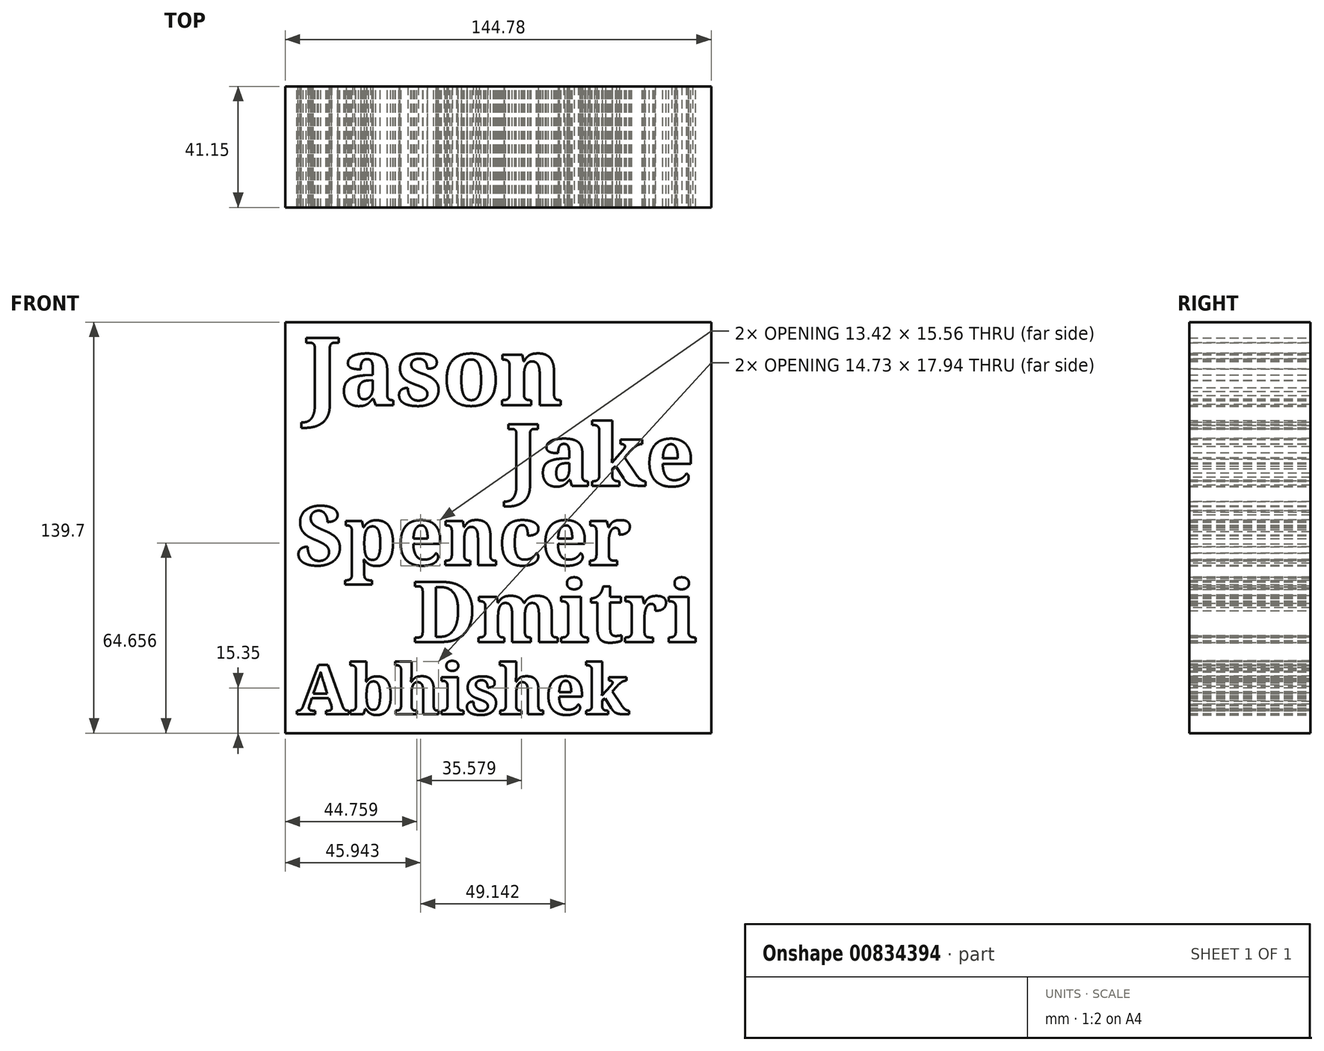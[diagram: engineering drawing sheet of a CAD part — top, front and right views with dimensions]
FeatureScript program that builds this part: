
annotation { "Feature Type Name" : "Feature", "Feature Type Description" : "" }
export const myFeature = defineFeature(function(context is Context, id is Id, definition is map)
    precondition{}
    {
        {
            var Q0;
            Q0=qCreatedBy(makeId("Front.planeOp"),FACE);
            var sketch = newSketch(context, id + "F0", { "sketchPlane" : qUnion([Q0])});
            skLineSegment(sketch, "E0.bottom", {"start": v(72.4, -69.85) * mm, "end": v(-72.39, -69.85) * mm});
            skLineSegment(sketch, "E0.top", {"start": v(72.39, 69.85) * mm, "end": v(-72.4, 69.85) * mm});
            skLineSegment(sketch, "E0.left", {"start": v(72.4, -69.85) * mm, "end": v(72.39, 69.85) * mm});
            skLineSegment(sketch, "E0.right", {"start": v(-72.39, -69.85) * mm, "end": v(-72.4, 69.85) * mm});
            skPoint(sketch, "E0.middle", {"position": v(0, 0) * mm});
            skText(sketch, "E1", { "text": "Jason", "fontName": "NotoSerif-Bold.ttf"});
            skText(sketch, "E2", { "text": "Jake", "fontName": "NotoSerif-Bold.ttf"});
            skText(sketch, "E3", { "text": "Spencer", "fontName": "NotoSerif-Bold.ttf"});
            skText(sketch, "E4", { "text": "Abhishek", "fontName": "NotoSerif-Bold.ttf"});
            skText(sketch, "E5", { "text": "Dmitri", "fontName": "NotoSerif-Bold.ttf"});
            const initialGuessF0  = {"E1": [-0.0657, 0.04161, 1, 0, 0.0231], "E2": [0.00308, 0.0142, 1, 0, 0.02107], "E3": [-0.06874, -0.0127, 1, 0, 0.02005], "E4": [-0.0685, -0.06347, 1, 0, 0.017], "E5": [-0.02915, -0.03885, 1, 0, 0.02056]};
            skSetInitialGuess(sketch, initialGuessF0);
            skSolve(sketch);
        }
        {
            var Q0;
            Q0=makeQuery(id+"F0.imprint","IMPRINT",FACE,{"disambiguationData":[TD([[makeQuery(id+"F0.imprint","IMPRINT",EDGE,{"derivedFrom":sQuery(id+"F0.wireOp",EDGE,"E0.bottom")}),-1.0]])]});
            var Q1;
            Q1=makeQuery(id+"F0.imprint","IMPRINT",FACE,{"disambiguationData":[TD([[makeQuery(id+"F0.imprint","IMPRINT",EDGE,{"derivedFrom":sQuery(id+"F0.wireOp",EDGE,"E1.sketch_text.stroke-28")}),1.0]])]});
            var Q2;
            Q2=makeQuery(id+"F0.imprint","IMPRINT",FACE,{"disambiguationData":[TD([[makeQuery(id+"F0.imprint","IMPRINT",EDGE,{"derivedFrom":sQuery(id+"F0.wireOp",EDGE,"E1.sketch_text.stroke-144")}),1.0]])]});
            var Q3;
            Q3=makeQuery(id+"F0.imprint","IMPRINT",FACE,{"disambiguationData":[TD([[makeQuery(id+"F0.imprint","IMPRINT",EDGE,{"derivedFrom":sQuery(id+"F0.wireOp",EDGE,"E2.sketch_text.stroke-28")}),1.0]])]});
            var Q4;
            Q4=makeQuery(id+"F0.imprint","IMPRINT",FACE,{"disambiguationData":[TD([[makeQuery(id+"F0.imprint","IMPRINT",EDGE,{"derivedFrom":sQuery(id+"F0.wireOp",EDGE,"E2.sketch_text.stroke-129")}),1.0]])]});
            var Q5;
            Q5=makeQuery(id+"F0.imprint","IMPRINT",FACE,{"disambiguationData":[TD([[makeQuery(id+"F0.imprint","IMPRINT",EDGE,{"derivedFrom":sQuery(id+"F0.wireOp",EDGE,"E3.sketch_text.stroke-229")}),1.0]])]});
            var Q6;
            Q6=makeQuery(id+"F0.imprint","IMPRINT",FACE,{"disambiguationData":[TD([[makeQuery(id+"F0.imprint","IMPRINT",EDGE,{"derivedFrom":sQuery(id+"F0.wireOp",EDGE,"E3.sketch_text.stroke-110")}),1.0]])]});
            var Q7;
            Q7=makeQuery(id+"F0.imprint","IMPRINT",FACE,{"disambiguationData":[TD([[makeQuery(id+"F0.imprint","IMPRINT",EDGE,{"derivedFrom":sQuery(id+"F0.wireOp",EDGE,"E3.sketch_text.stroke-98")}),1.0]])]});
            var Q8;
            Q8=makeQuery(id+"F0.imprint","IMPRINT",FACE,{"disambiguationData":[TD([[makeQuery(id+"F0.imprint","IMPRINT",EDGE,{"derivedFrom":sQuery(id+"F0.wireOp",EDGE,"E4.sketch_text.stroke-83")}),1.0]])]});
            var Q9;
            Q9=makeQuery(id+"F0.imprint","IMPRINT",FACE,{"disambiguationData":[TD([[makeQuery(id+"F0.imprint","IMPRINT",EDGE,{"derivedFrom":sQuery(id+"F0.wireOp",EDGE,"E4.sketch_text.stroke-36")}),1.0]])]});
            var Q10;
            Q10=makeQuery(id+"F0.imprint","IMPRINT",FACE,{"disambiguationData":[TD([[makeQuery(id+"F0.imprint","IMPRINT",EDGE,{"derivedFrom":sQuery(id+"F0.wireOp",EDGE,"E4.sketch_text.stroke-289")}),1.0]])]});
            var Q11;
            Q11=makeQuery(id+"F0.imprint","IMPRINT",FACE,{"disambiguationData":[TD([[makeQuery(id+"F0.imprint","IMPRINT",EDGE,{"derivedFrom":sQuery(id+"F0.wireOp",EDGE,"E5.sketch_text.stroke-23")}),1.0]])]});
            extrude(context, id + "F1", {"entities" : qUnion([Q0, Q1, Q2, Q3, Q4, Q5, Q6, Q7, Q8, Q9, Q10, Q11]), "depth" : 41.15 * mm, "offsetDistance" : 25.4 * mm});
        }
    });
